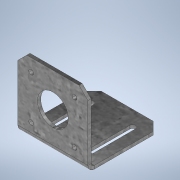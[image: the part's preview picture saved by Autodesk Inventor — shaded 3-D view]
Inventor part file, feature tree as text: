
AUTODESK INVENTOR PART (.ipt)
format: ipt  version: 2022 (Build 260153000, 153)  size: 167,424 bytes
history: native  units: in
note: dims shown in document units (in); Inventor stores cm internally (conversion verified against a paired STEP export)
features: sheet_metal_op x2, hole x2, other x2, sketch x1
ambient origin geometry x8: Origin, YZ Plane, XZ Plane, XY Plane, X Axis, Y Axis, Z Axis, Center Point
bodies: Solid1 (feature_tree)
feature tree (7):
  sketch  "Sketch1"  dims[d0=1.9685in d1=3.937in d2=1.1811in d3=0.0827in d4=0.4331in d5=1.1811in d6=1.9291in d7=1.2205in d8=1.2205in d9=0.09in d10=0.09in d11=0.045in d12=0.18in d13=0.09in d14=90.0deg d15=0.09in d16=0.1339in d17=0.75in d18=0.256in d19=0.118in d20=90.0deg d21=0.09in d22=0.8108in d23=0.8661in d24=0.75in d25=0.375in d26=0.25in d27=0.5635in d28=1.0in d29=0.8108in d30=0.25in d31=0.25in d32=45.0deg]
  sheet_metal_op  "Face1"
  sheet_metal_op  "Fold1"
  hole  "Hole1"  [1 undecoded]
  hole  "Hole2"  [1 undecoded]
  other  "Corner Chamfer1"
  other  "Plate1"
note: 2 required parameter values undecoded (feature->parameter linkage not recoverable at this tier; creation-order binding heuristic only, values carry confidence <= 0.55)
